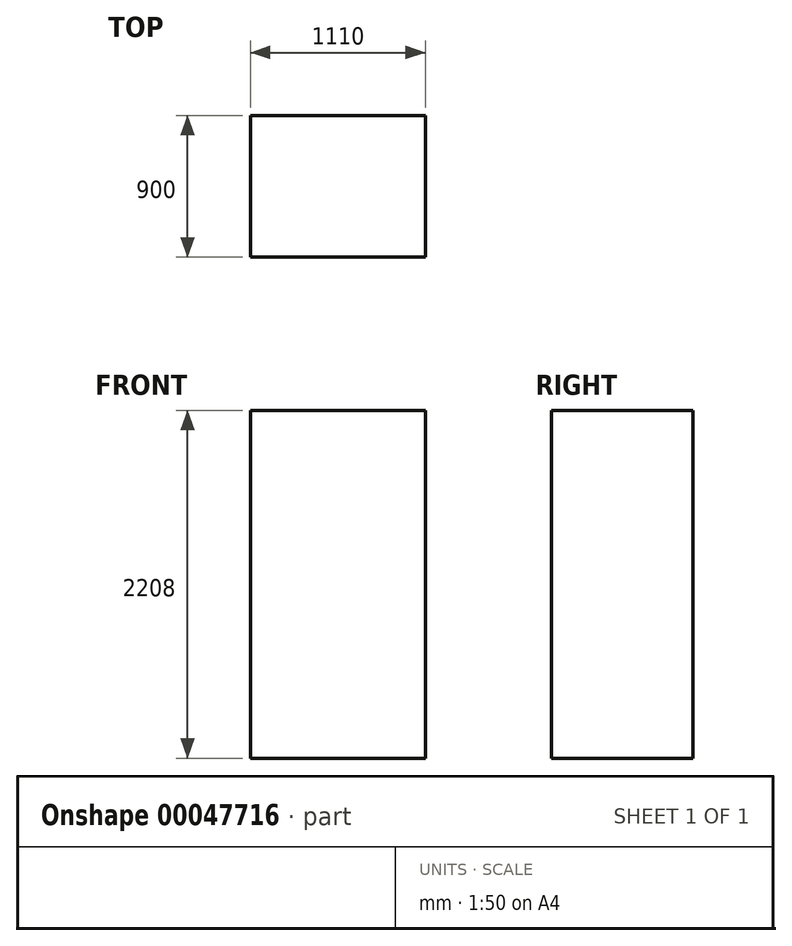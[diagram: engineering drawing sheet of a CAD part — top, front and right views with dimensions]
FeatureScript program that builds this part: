
annotation { "Feature Type Name" : "Feature", "Feature Type Description" : "" }
export const myFeature = defineFeature(function(context is Context, id is Id, definition is map)
    precondition{}
    {
        {
            var Q0;
            Q0=qCreatedBy(makeId("Front.planeOp"),FACE);
            var sketch = newSketch(context, id + "F0", { "sketchPlane" : qUnion([Q0])});
            skLineSegment(sketch, "E0.bottom", {"start": v(0, 0) * mm, "end": v(1110, 0) * mm});
            skLineSegment(sketch, "E0.top", {"start": v(0, -2208) * mm, "end": v(1110, -2208) * mm});
            skLineSegment(sketch, "E0.left", {"start": v(0, 0) * mm, "end": v(0, -2208) * mm});
            skLineSegment(sketch, "E0.right", {"start": v(1110, 0) * mm, "end": v(1110, -2208) * mm});
            skSolve(sketch);
        }
        {
            var Q0;
            Q0 = qSketchRegion(id + "F0", true);
            extrude(context, id + "F1", {"entities" : qUnion([Q0]), "depth" : 900 * mm});
        }
    });
